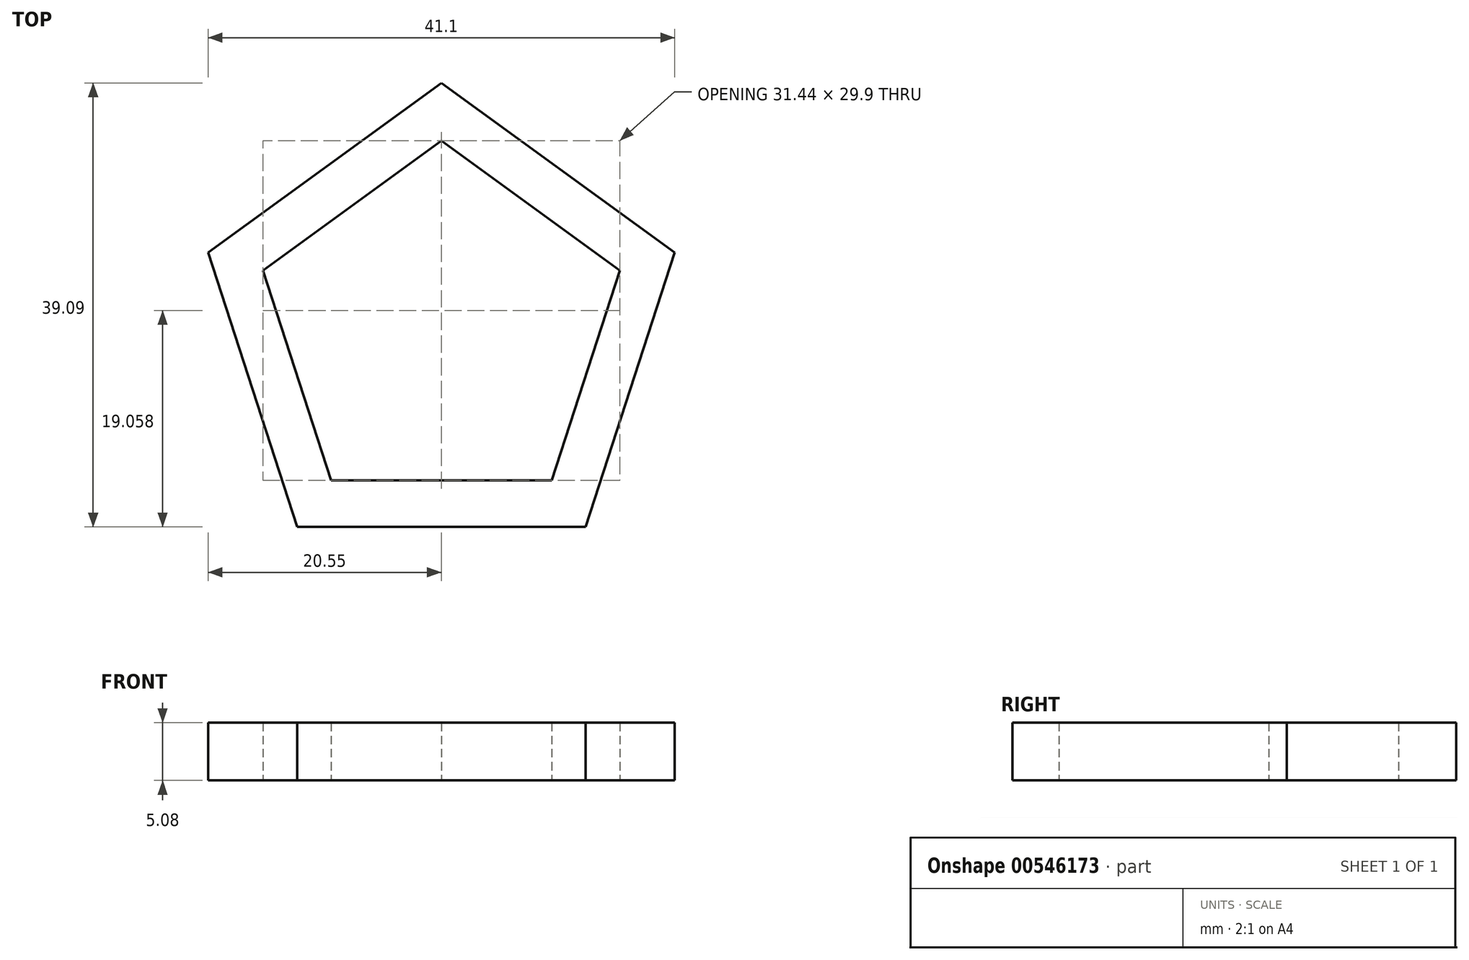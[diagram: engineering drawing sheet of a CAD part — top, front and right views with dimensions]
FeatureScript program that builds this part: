
annotation { "Feature Type Name" : "Feature", "Feature Type Description" : "" }
export const myFeature = defineFeature(function(context is Context, id is Id, definition is map)
    precondition{}
    {
        {
            var Q0;
            Q0=qCreatedBy(makeId("Top.planeOp"),FACE);
            var sketch = newSketch(context, id + "F0", { "sketchPlane" : qUnion([Q0])});
            skLineSegment(sketch, "E0", {"start": v(0, 0) * mm, "end": v(25.4, 0) * mm});
            skLineSegment(sketch, "E1", {"start": v(0, 0) * mm, "end": v(-7.85, 24.16) * mm});
            skLineSegment(sketch, "E2", {"start": v(-7.85, 24.16) * mm, "end": v(12.7, 39.09) * mm});
            skLineSegment(sketch, "E3", {"start": v(12.7, 39.09) * mm, "end": v(33.25, 24.16) * mm});
            skLineSegment(sketch, "E4", {"start": v(33.25, 24.16) * mm, "end": v(25.4, 0) * mm});
            skLineSegment(sketch, "E5", {"start": v(-7.85, 24.16) * mm, "end": v(-3.02, 22.59) * mm});
            skLineSegment(sketch, "E6", {"start": v(0, 0) * mm, "end": v(2.99, 4.1) * mm});
            skLineSegment(sketch, "E7", {"start": v(25.4, 0) * mm, "end": v(22.41, 4.1) * mm});
            skLineSegment(sketch, "E8", {"start": v(33.25, 24.16) * mm, "end": v(28.42, 22.59) * mm});
            skLineSegment(sketch, "E9", {"start": v(12.7, 39.09) * mm, "end": v(12.7, 34) * mm});
            skLineSegment(sketch, "E10", {"start": v(-3.02, 22.59) * mm, "end": v(2.99, 4.1) * mm});
            skLineSegment(sketch, "E11", {"start": v(22.41, 4.1) * mm, "end": v(2.99, 4.1) * mm});
            skLineSegment(sketch, "E12", {"start": v(28.42, 22.59) * mm, "end": v(22.41, 4.1) * mm});
            skLineSegment(sketch, "E13", {"start": v(28.42, 22.59) * mm, "end": v(12.7, 34) * mm});
            skLineSegment(sketch, "E14", {"start": v(12.7, 34) * mm, "end": v(-3.02, 22.59) * mm});
            skSolve(sketch);
        }
        {
            var Q0;
            Q0=makeQuery(id+"F0.imprint","IMPRINT",FACE,{"disambiguationData":[TD([[makeQuery(id+"F0.imprint","IMPRINT",EDGE,{"derivedFrom":sQuery(id+"F0.wireOp",EDGE,"E2")}),-1.0]])]});
            var Q1;
            Q1=makeQuery(id+"F0.imprint","IMPRINT",FACE,{"disambiguationData":[TD([[makeQuery(id+"F0.imprint","IMPRINT",EDGE,{"derivedFrom":sQuery(id+"F0.wireOp",EDGE,"E1")}),-1.0]])]});
            var Q2;
            Q2=makeQuery(id+"F0.imprint","IMPRINT",FACE,{"disambiguationData":[TD([[makeQuery(id+"F0.imprint","IMPRINT",EDGE,{"derivedFrom":sQuery(id+"F0.wireOp",EDGE,"E0")}),1.0]])]});
            var Q3;
            Q3=makeQuery(id+"F0.imprint","IMPRINT",FACE,{"disambiguationData":[TD([[makeQuery(id+"F0.imprint","IMPRINT",EDGE,{"derivedFrom":sQuery(id+"F0.wireOp",EDGE,"E4")}),-1.0]])]});
            var Q4;
            Q4=makeQuery(id+"F0.imprint","IMPRINT",FACE,{"disambiguationData":[TD([[makeQuery(id+"F0.imprint","IMPRINT",EDGE,{"derivedFrom":sQuery(id+"F0.wireOp",EDGE,"E3")}),-1.0]])]});
            extrude(context, id + "F1", {"entities" : qUnion([Q0, Q1, Q2, Q3, Q4]), "depth" : 5.08 * mm, "offsetDistance" : 25.4 * mm});
        }
    });
